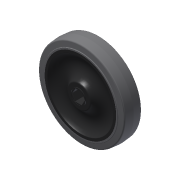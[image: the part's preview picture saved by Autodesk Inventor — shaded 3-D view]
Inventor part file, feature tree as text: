
AUTODESK INVENTOR PART (.ipt)
format: ipt  version: 2015 (Build 190159000, 159)  size: 304,128 bytes
history: native  units: in
note: dims shown in document units (in); Inventor stores cm internally (conversion verified against a paired STEP export)
features: revolve x1, other x1, imported_body x1
ambient origin geometry x8: Origin, YZ Plane, XZ Plane, XY Plane, X Axis, Y Axis, Z Axis, Center Point
bodies: Body1 (feature_tree)
feature tree (3):
  revolve  "Revolve1"  [1 undecoded]
  other  "217-4049-STEP-201410301"
  imported_body  "Base1"
note: 1 required parameter value undecoded (feature->parameter linkage not recoverable at this tier; creation-order binding heuristic only, values carry confidence <= 0.55)
